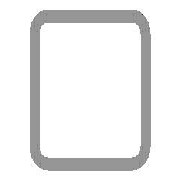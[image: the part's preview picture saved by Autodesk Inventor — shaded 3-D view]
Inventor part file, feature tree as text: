
AUTODESK INVENTOR PART (.ipt)
format: ipt  version: 2025 (Build 290162010, 162A)  size: 131,072 bytes
history: native  units: mm (DEFAULTED — no unit token found)
features: other x3, sketch x1, plane x1
ambient origin geometry x8: Origin, YZ Plane, XZ Plane, XY Plane, X Axis, Y Axis, Z Axis, Center Point
bodies: Solid1 (feature_tree), Body (feature_tree)
feature tree (5):
  other  "Driven Length"
  other  "Start plane"
  other  "End plane"
  sketch  "Sketch3"  dims[d3=2925.0mm d4=0.0mm d7=6.0mm d9=80.0mm d11=80.0mm d12=3.0mm d13=-0.0mm d14=2925.0mm d15=40.0mm d16=40.0mm d17=90.0deg d18=2925.0mm]
  plane  "Work Plane3"
